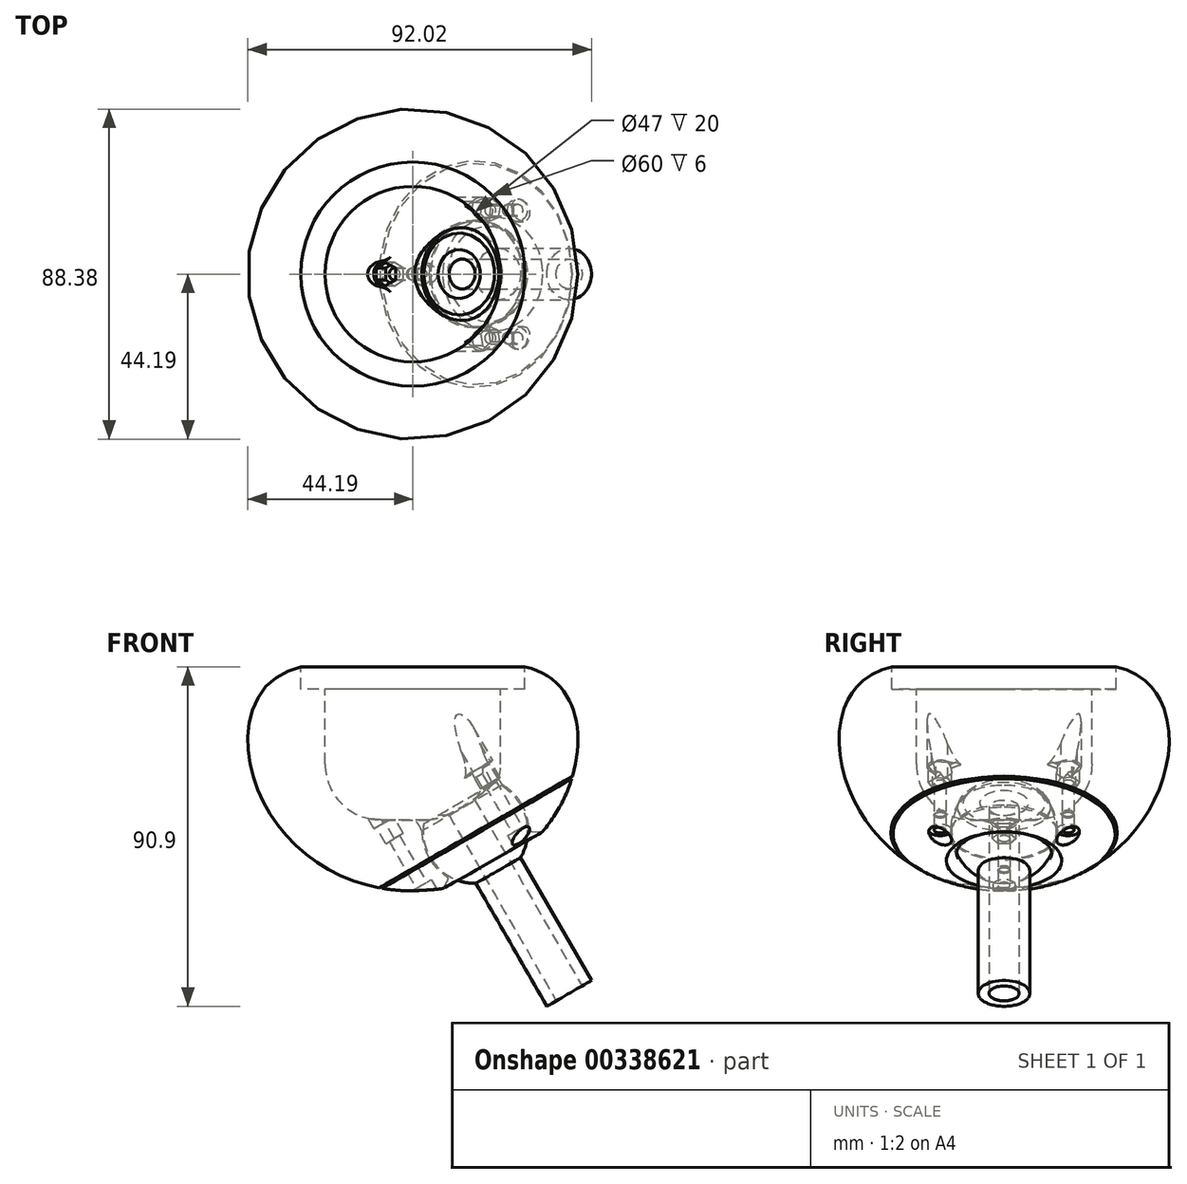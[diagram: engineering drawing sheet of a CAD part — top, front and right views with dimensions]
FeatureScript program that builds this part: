
annotation { "Feature Type Name" : "Feature", "Feature Type Description" : "" }
export const myFeature = defineFeature(function(context is Context, id is Id, definition is map)
    precondition{}
    {
        {
            var Q0;
            Q0=qCreatedBy(makeId("Front.planeOp"),FACE);
            var sketch = newSketch(context, id + "F0", { "sketchPlane" : qUnion([Q0])});
            skLineSegment(sketch, "E0", {"start": v(23.5, 32.37) * mm, "end": v(30, 32.37) * mm});
            skLineSegment(sketch, "E1", {"start": v(30, 32.37) * mm, "end": v(30, 38.37) * mm});
            skLineSegment(sketch, "E2", {"start": v(23.5, 32.37) * mm, "end": v(23.5, 12.37) * mm});
            skLineSegment(sketch, "E3", {"start": v(8.5, -2.63) * mm, "end": v(0, -2.63) * mm});
            skArc(sketch, "E4.filletArc", {"start": v(8.5, -2.63) * mm, "mid": v(19.1, 1.77) * mm, "end": v(23.5, 12.37) * mm});
            skLineSegment(sketch, "E5", {"start": v(43, 48.23) * mm, "end": v(43, -18) * mm, "construction": true});
            skLineSegment(sketch, "E6", {"start": v(0, 64.06) * mm, "end": v(0, 13.27) * mm, "construction": true});
            skPoint(sketch, "E7", {"position": v(43, 36.55) * mm});
            skPoint(sketch, "E8", {"position": v(43, 10.04) * mm});
            skFitSpline(sketch, "E9", {"points": [v(30, 38.37) * mm, v(43, 10.04) * mm, v(0, -21.63) * mm], "startDerivative": vector(90.04, -20.78) * mm, "endDerivative": vector(-121.99, 0) * mm});
            skPoint(sketch, "E10", {"position": v(30, 35.37) * mm});
            skLineSegment(sketch, "E11", {"start": v(0, -2.63) * mm, "end": v(0, -21.63) * mm});
            skSolve(sketch);
        }
        {
            var Q0;
            Q0=qCreatedBy(makeId("Front.planeOp"),FACE);
            var sketch = newSketch(context, id + "F1", { "sketchPlane" : qUnion([Q0])});
            skArc(sketch, "E12", {"start": v(31.35, -6.1) * mm, "mid": v(24.2, 6.35) * mm, "end": v(9.84, 6.36) * mm});
            skLineSegment(sketch, "E13", {"start": v(31.35, -6.1) * mm, "end": v(53.04, -7.04) * mm});
            skLineSegment(sketch, "E14", {"start": v(53.04, -7.04) * mm, "end": v(26.44, -22.4) * mm});
            skLineSegment(sketch, "E15", {"start": v(26.44, -22.4) * mm, "end": v(9.84, 6.36) * mm});
            skLineSegment(sketch, "E16", {"start": v(45.56, -47.51) * mm, "end": v(16.88, 2.16) * mm});
            skLineSegment(sketch, "E17", {"start": v(16.88, 2.16) * mm, "end": v(18.37, 4.75) * mm});
            skArc(sketch, "E18", {"start": v(29.08, -13.15) * mm, "mid": v(30.25, -1.52) * mm, "end": v(22.2, 6.95) * mm});
            skLineSegment(sketch, "E19", {"start": v(29.08, -13.15) * mm, "end": v(48.08, -46.06) * mm});
            skLineSegment(sketch, "E20", {"start": v(48.08, -46.06) * mm, "end": v(45.56, -47.51) * mm});
            skCircle(sketch, "E21", {"center": v(0, 23.4) * mm, "radius": 45.03 * mm, "construction": true});
            skLineSegment(sketch, "E22", {"start": v(18.37, 4.75) * mm, "end": v(22.2, 6.95) * mm});
            skArc(sketch, "E23", {"start": v(22.38, 13.92) * mm, "mid": v(22.45, 9.93) * mm, "end": v(24.2, 6.35) * mm});
            skLineSegment(sketch, "E24", {"start": v(22.38, 13.92) * mm, "end": v(9.84, 6.36) * mm});
            skLineSegment(sketch, "E25", {"start": v(-20.59, -27.76) * mm, "end": v(69.48, 24.24) * mm, "construction": true});
            skSolve(sketch);
        }
        {
            var Q0;
            Q0=qCreatedBy(makeId("Front.planeOp"),FACE);
            var sketch = newSketch(context, id + "F2", { "sketchPlane" : qUnion([Q0])});
            skLineSegment(sketch, "E26", {"start": v(-20.46, -27.98) * mm, "end": v(-20.71, -27.55) * mm});
            skLineSegment(sketch, "E27", {"start": v(-20.71, -27.55) * mm, "end": v(69.35, 24.45) * mm});
            skLineSegment(sketch, "E28", {"start": v(69.35, 24.45) * mm, "end": v(69.6, 24.02) * mm});
            skLineSegment(sketch, "E29", {"start": v(69.6, 24.02) * mm, "end": v(-20.46, -27.98) * mm});
            skSolve(sketch);
        }
        {
            var Q0;
            Q0=makeQuery(id+"F0.imprint","IMPRINT",FACE,{"disambiguationData":[TD([[makeQuery(id+"F0.imprint","IMPRINT",EDGE,{"derivedFrom":sQuery(id+"F0.wireOp",EDGE,"E0")}),-1.0]])]});
            var Q1;
            {var subQ6=sQuery(id+"F0.wireOp",EDGE,"E3");Q1=makeQuery(id+"F0.imprint","IMPRINT",FACE,{"disambiguationData":[TD([[makeQuery(id+"F0.imprint","IMPRINT",EDGE,{"derivedFrom":subQ6}),1.0]])]});}
            var Q2;
            {var subQ1=sQuery(id+"F0.wireOp",EDGE,"KXl2rAyY-RLrS-Eotx-2UTr-zvvv9nwZEpHV");var subQ3=sQuery(id+"F0.wireOp",EDGE,"E4.filletArc");var subQ4=makeQuery(id+"F0.imprint","INTERSECT",VERTEX,{"derivedFrom":[subQ3,subQ1]});Q2=makeQuery(id+"F0.imprint","IMPRINT",FACE,{"disambiguationData":[TD([[makeQuery(id+"F0.imprint","IMPRINT",EDGE,{"disambiguationData":[TD([[subQ4,1.0]])],"derivedFrom":subQ3}),-1.0]])]});}
            var Q3;
            {var subQ0=sQuery(id+"F0.wireOp",EDGE,"lHVRG2s5-drey-582v-L7Ij-X5NfUEFu1qqW");var subQ3=sQuery(id+"F0.wireOp",EDGE,"E4.filletArc");var subQ4=makeQuery(id+"F0.imprint","INTERSECT",VERTEX,{"derivedFrom":[subQ3,subQ0]});Q3=makeQuery(id+"F0.imprint","IMPRINT",FACE,{"disambiguationData":[TD([[makeQuery(id+"F0.imprint","IMPRINT",EDGE,{"disambiguationData":[TD([[subQ4,-1.0]])],"derivedFrom":subQ3}),-1.0]])]});}
            var Q4;
            {var subQ5=sQuery(id+"F0.wireOp",EDGE,"lHVRG2s5-drey-582v-L7Ij-X5NfUEFu1qqW");Q4=makeQuery(id+"F0.imprint","IMPRINT",FACE,{"disambiguationData":[TD([[makeQuery(id+"F0.imprint","IMPRINT",EDGE,{"derivedFrom":subQ5}),-1.0]])]});}
            var Q5;
            Q5=sQuery(id+"F0.wireOp",EDGE,"E6");
            revolve(context, id + "F3", {"entities" : qUnion([Q0, Q1, Q2, Q3, Q4]), "axis" : qUnion([Q5]), "revolveType" : RevolveType.FULL});
        }
        {
            var Q0;
            Q0=qSketchRegion(id+"F2",true);
            extrude(context, id + "F4", {"entities" : qUnion([Q0]), "operationType" : NewBodyOperationType.REMOVE, "endBound" : BoundingType.THROUGH_ALL, "oppositeDirection" : true, "depth" : 25 * mm, "hasSecondDirection" : true, "secondDirectionBound" : BoundingType.THROUGH_ALL, "secondDirectionOppositeDirection" : false, "secondDirectionDepth" : 25 * mm});
        }
        {
            var Q0;
            Q0=makeQuery(id+"F4.boolean.opBoolean","SPLIT",BODY,{"disambiguationData":[OD(1.0)],"derivedFrom":makeQuery(id+"F3.opRevolve","SWEPT_BODY",BODY,{"disambiguationData":[OSD([sQuery(id+"F0.wireOp",EDGE,"E0"),sQuery(id+"F0.wireOp",EDGE,"E1"),sQuery(id+"F0.wireOp",EDGE,"E2"),sQuery(id+"F0.wireOp",EDGE,"E3"),sQuery(id+"F0.wireOp",EDGE,"E4.filletArc"),sQuery(id+"F0.wireOp",EDGE,"E9"),sQuery(id+"F0.wireOp",EDGE,"E11")])]})});
            var Q1;
            Q1=sQuery(id+"F1.wireOp",EDGE,"E15");
            transform(context, id + "F5", {"entities" : qUnion([Q0]), "transformType" : TransformType.TRANSLATION_DISTANCE, "transformDirection" : qUnion([Q1]), "distance" : 0.5 * mm, "oppositeDirection" : true, "makeCopy" : false});
        }
        {
            var Q0;
            {var subQ0=sQuery(id+"F1.wireOp",EDGE,"E23");var subQ1=sQuery(id+"F1.wireOp",EDGE,"E12");var subQ2=makeQuery(id+"F1.imprint","INTERSECT",VERTEX,{"disambiguationData":[OD(1.0)],"derivedFrom":[subQ1,subQ0]});Q0=makeQuery(id+"F1.imprint","IMPRINT",FACE,{"disambiguationData":[TD([[makeQuery(id+"F1.imprint","IMPRINT",EDGE,{"disambiguationData":[TD([[subQ2,-1.0]])],"derivedFrom":subQ1}),-1.0]])]});}
            var Q1;
            {var subQ8=sQuery(id+"F1.wireOp",EDGE,"E13");Q1=makeQuery(id+"F1.imprint","IMPRINT",FACE,{"disambiguationData":[TD([[makeQuery(id+"F1.imprint","IMPRINT",EDGE,{"derivedFrom":subQ8}),-1.0]])]});}
            var Q2;
            {var subQ1=sQuery(id+"F1.wireOp",EDGE,"E17");Q2=makeQuery(id+"F1.imprint","IMPRINT",FACE,{"disambiguationData":[TD([[makeQuery(id+"F1.imprint","IMPRINT",EDGE,{"derivedFrom":subQ1}),-1.0]])]});}
            var Q3;
            Q3=sQuery(id+"F1.wireOp",EDGE,"E15");
            revolve(context, id + "F6", {"operationType" : NewBodyOperationType.REMOVE, "entities" : qUnion([Q0, Q1, Q2]), "axis" : qUnion([Q3]), "revolveType" : RevolveType.FULL, "oppositeDirection" : true});
        }
        {
            var Q0;
            {var subQ1=sQuery(id+"F1.wireOp",EDGE,"E17");Q0=makeQuery(id+"F1.imprint","IMPRINT",FACE,{"disambiguationData":[TD([[makeQuery(id+"F1.imprint","IMPRINT",EDGE,{"derivedFrom":subQ1}),-1.0]])]});}
            var Q1;
            {var subQ5=sQuery(id+"F1.wireOp",EDGE,"E20");Q1=makeQuery(id+"F1.imprint","IMPRINT",FACE,{"disambiguationData":[TD([[makeQuery(id+"F1.imprint","IMPRINT",EDGE,{"derivedFrom":subQ5}),-1.0]])]});}
            var Q2;
            Q2=sQuery(id+"F1.wireOp",EDGE,"E15");
            revolve(context, id + "F7", {"entities" : qUnion([Q0, Q1]), "axis" : qUnion([Q2]), "revolveType" : RevolveType.FULL});
        }
        {
            var Q0;
            Q0=makeQuery(id+"F6.boolean.opBoolean","COPY",EDGE,{"derivedFrom":makeQuery(id+"F6.opRevolve","SWEPT_EDGE",EDGE,{"disambiguationData":[OSD([sQuery(id+"F1.wireOp",EDGE,"E12"),sQuery(id+"F1.wireOp",EDGE,"E13")])]})});
            var Q1;
            Q1=makeQuery(id+"F6.boolean.opBoolean","INTERSECT",EDGE,{"derivedFrom":[makeQuery(id+"F3.opRevolve","SWEPT_FACE",FACE,{"disambiguationData":[OSD([sQuery(id+"F0.wireOp",EDGE,"E4.filletArc")])]}),makeQuery(id+"F6.opRevolve","SWEPT_FACE",FACE,{"disambiguationData":[OSD([sQuery(id+"F1.wireOp",EDGE,"E12")])]})]});
            fillet(context, id + "F8", {"entities" : qUnion([Q0, Q1]), "radius" : 1 * mm, "tangentPropagation" : true, "allowEdgeOverflow" : false});
        }
        {
            var Q0;
            Q0=makeQuery(id+"F4.boolean.opBoolean","COPY",FACE,{"derivedFrom":makeQuery(id+"F4.opExtrude","SWEPT_FACE",FACE,{"disambiguationData":[OSD([sQuery(id+"F2.wireOp",EDGE,"E27")])]})});
            cPlane(context, id + "F9", {"entities" : qUnion([Q0]), "cplaneType" : CPlaneType.OFFSET, "offset" : 16.6 * mm, "width" : 150 * mm, "height" : 150 * mm});
        }
        {
            var Q0;
            Q0=qCreatedBy(id+"F9.planeOp",FACE);
            var sketch = newSketch(context, id + "F10", { "sketchPlane" : qUnion([Q0])});
            skLineSegment(sketch, "E30", {"start": v(-2.62, 0) * mm, "end": v(-18.22, 0) * mm, "construction": true});
            skCircle(sketch, "E31", {"center": v(-8.07, 0) * mm, "radius": 1.6 * mm});
            skCircle(sketch, "E32", {"center": v(-8.07, 0) * mm, "radius": 3.05 * mm});
            skPoint(sketch, "E33", {"position": v(11.7, 0) * mm});
            skCircle(sketch, "E34.1.0", {"center": v(21.6, -17.13) * mm, "radius": 3.05 * mm});
            skCircle(sketch, "E34.1.1", {"center": v(21.6, -17.13) * mm, "radius": 1.6 * mm});
            skCircle(sketch, "E34.2.0", {"center": v(21.6, 17.13) * mm, "radius": 3.05 * mm});
            skCircle(sketch, "E34.2.1", {"center": v(21.6, 17.13) * mm, "radius": 1.6 * mm});
            skSolve(sketch);
        }
        {
            var Q0;
            Q0=makeQuery(id+"F10.imprint","IMPRINT",FACE,{"disambiguationData":[TD([[makeQuery(id+"F10.imprint","IMPRINT",EDGE,{"derivedFrom":sQuery(id+"F10.wireOp",EDGE,"E34.2.1")}),1.0]])]});
            var Q1;
            Q1=makeQuery(id+"F10.imprint","IMPRINT",FACE,{"disambiguationData":[TD([[makeQuery(id+"F10.imprint","IMPRINT",EDGE,{"derivedFrom":sQuery(id+"F10.wireOp",EDGE,"E34.1.1")}),1.0]])]});
            var Q2;
            Q2=makeQuery(id+"F10.imprint","IMPRINT",FACE,{"disambiguationData":[TD([[makeQuery(id+"F10.imprint","IMPRINT",EDGE,{"derivedFrom":sQuery(id+"F10.wireOp",EDGE,"E31")}),1.0]])]});
            extrude(context, id + "F11", {"entities" : qUnion([Q0, Q1, Q2]), "operationType" : NewBodyOperationType.REMOVE, "oppositeDirection" : true, "depth" : 31 * mm});
        }
        {
            var Q0;
            Q0=makeQuery(id+"F10.imprint","IMPRINT",FACE,{"disambiguationData":[TD([[makeQuery(id+"F10.imprint","IMPRINT",EDGE,{"derivedFrom":sQuery(id+"F10.wireOp",EDGE,"E34.1.0")}),1.0]])]});
            var Q1;
            Q1=makeQuery(id+"F10.imprint","IMPRINT",FACE,{"disambiguationData":[TD([[makeQuery(id+"F10.imprint","IMPRINT",EDGE,{"derivedFrom":sQuery(id+"F10.wireOp",EDGE,"E31")}),-1.0]])]});
            var Q2;
            Q2=makeQuery(id+"F10.imprint","IMPRINT",FACE,{"disambiguationData":[TD([[makeQuery(id+"F10.imprint","IMPRINT",EDGE,{"derivedFrom":sQuery(id+"F10.wireOp",EDGE,"E34.2.0")}),1.0]])]});
            extrude(context, id + "F12", {"entities" : qUnion([Q0, Q1, Q2]), "operationType" : NewBodyOperationType.REMOVE, "oppositeDirection" : true, "depth" : 11.5 * mm});
        }
        {
            var Q0;
            Q0=makeQuery(id+"F11.boolean.opBoolean","COPY",FACE,{"derivedFrom":makeQuery(id+"F11.opExtrude","CAP_FACE",FACE,{"disambiguationData":[OSD([sQuery(id+"F10.wireOp",EDGE,"E31")])],"isStart":false})});
            cPlane(context, id + "F13", {"entities" : qUnion([Q0]), "cplaneType" : CPlaneType.OFFSET, "offset" : 0 * mm, "oppositeDirection" : true, "width" : 150 * mm, "height" : 150 * mm});
        }
        {
            var Q0;
            Q0=qCreatedBy(id+"F13.planeOp",FACE);
            var sketch = newSketch(context, id + "F14", { "sketchPlane" : qUnion([Q0])});
            skCircle(sketch, "E35.cCircle", {"center": v(21.6, 17.13) * mm, "radius": 2.75 * mm, "construction": true});
            skLineSegment(sketch, "E35.0", {"start": v(22.16, 20.25) * mm, "end": v(24.58, 18.2) * mm});
            skLineSegment(sketch, "E35.1", {"start": v(24.58, 18.2) * mm, "end": v(24.01, 15.07) * mm});
            skLineSegment(sketch, "E35.2", {"start": v(24.01, 15.07) * mm, "end": v(21.03, 14) * mm});
            skLineSegment(sketch, "E35.3", {"start": v(21.03, 14) * mm, "end": v(18.6, 16.05) * mm});
            skLineSegment(sketch, "E35.4", {"start": v(18.6, 16.05) * mm, "end": v(19.17, 19.18) * mm});
            skLineSegment(sketch, "E35.5", {"start": v(19.17, 19.18) * mm, "end": v(22.16, 20.25) * mm});
            skPoint(sketch, "E35.0.midPoint", {"position": v(23.37, 19.22) * mm});
            skCircle(sketch, "E36.cCircle", {"center": v(-8.07, 0) * mm, "radius": 2.75 * mm, "construction": true});
            skLineSegment(sketch, "E36.0", {"start": v(-10.82, -1.59) * mm, "end": v(-10.82, 1.59) * mm});
            skLineSegment(sketch, "E36.1", {"start": v(-10.82, 1.59) * mm, "end": v(-8.07, 3.18) * mm});
            skLineSegment(sketch, "E36.2", {"start": v(-8.07, 3.18) * mm, "end": v(-5.32, 1.59) * mm});
            skLineSegment(sketch, "E36.3", {"start": v(-5.32, 1.59) * mm, "end": v(-5.32, -1.59) * mm});
            skLineSegment(sketch, "E36.4", {"start": v(-5.32, -1.59) * mm, "end": v(-8.07, -3.18) * mm});
            skLineSegment(sketch, "E36.5", {"start": v(-8.07, -3.18) * mm, "end": v(-10.82, -1.59) * mm});
            skPoint(sketch, "E36.0.midPoint", {"position": v(-10.82, 0) * mm});
            skLineSegment(sketch, "E37", {"start": v(11.7, 0) * mm, "end": v(42.27, 0) * mm, "construction": true});
            skLineSegment(sketch, "E38.MirrorCS", {"start": v(22.16, -20.25) * mm, "end": v(24.58, -18.2) * mm});
            skLineSegment(sketch, "E39.MirrorCS", {"start": v(21.03, -14) * mm, "end": v(18.6, -16.05) * mm});
            skPoint(sketch, "E40.MirrorP", {"position": v(23.37, -19.22) * mm});
            skLineSegment(sketch, "E41.MirrorCS", {"start": v(24.01, -15.07) * mm, "end": v(21.03, -14) * mm});
            skLineSegment(sketch, "E42.MirrorCS", {"start": v(24.58, -18.2) * mm, "end": v(24.01, -15.07) * mm});
            skLineSegment(sketch, "E43.MirrorCS", {"start": v(18.6, -16.05) * mm, "end": v(19.17, -19.18) * mm});
            skLineSegment(sketch, "E44.MirrorCS", {"start": v(19.17, -19.18) * mm, "end": v(22.16, -20.25) * mm});
            skCircle(sketch, "E45.MirrorC", {"center": v(21.6, -17.13) * mm, "radius": 2.75 * mm, "construction": true});
            skSolve(sketch);
        }
        {
            var Q0;
            Q0=qSketchRegion(id+"F14",true);
            extrude(context, id + "F15", {"entities" : qUnion([Q0]), "operationType" : NewBodyOperationType.REMOVE, "depth" : 5 * mm});
        }
        {
            var Q0;
            Q0=qCreatedBy(id+"F13.planeOp",FACE);
            var sketch = newSketch(context, id + "F16", { "sketchPlane" : qUnion([Q0])});
            skCircle(sketch, "E46.2.0", {"center": v(21.6, -17.13) * mm, "radius": 3.5 * mm});
            skArc(sketch, "E47", {"start": v(19.04, -19.52) * mm, "mid": v(15.95, -18.24) * mm, "end": v(12.76, -19.26) * mm});
            skArc(sketch, "E48", {"start": v(25.13, -8.5) * mm, "mid": v(23.8, -11.72) * mm, "end": v(24.47, -15.14) * mm});
            skLineSegment(sketch, "E49", {"start": v(25.13, -8.5) * mm, "end": v(12.76, -19.26) * mm});
            skPoint(sketch, "E50", {"position": v(11.7, 0) * mm});
            skArc(sketch, "E51.MirrorCS", {"start": v(19.04, 19.52) * mm, "mid": v(15.95, 18.24) * mm, "end": v(12.76, 19.26) * mm});
            skArc(sketch, "E52.MirrorCS", {"start": v(25.13, 8.5) * mm, "mid": v(23.8, 11.72) * mm, "end": v(24.47, 15.14) * mm});
            skLineSegment(sketch, "E53.MirrorCS", {"start": v(25.13, 8.5) * mm, "end": v(12.76, 19.26) * mm});
            skCircle(sketch, "E54.MirrorC", {"center": v(21.6, 17.13) * mm, "radius": 3.5 * mm});
            skCircle(sketch, "E55", {"center": v(-8.07, 0) * mm, "radius": 3.5 * mm});
            skArc(sketch, "E56", {"start": v(-5.4, -6.7) * mm, "mid": v(-6.42, -4.63) * mm, "end": v(-8.43, -3.48) * mm});
            skArc(sketch, "E57", {"start": v(-8.58, 3.46) * mm, "mid": v(-6.35, 4.99) * mm, "end": v(-5.63, 7.6) * mm});
            skLineSegment(sketch, "E58", {"start": v(-5.4, -6.7) * mm, "end": v(-5.63, 7.6) * mm});
            skSolve(sketch);
        }
        {
            var Q0;
            Q0=qSketchRegion(id+"F16",true);
            extrude(context, id + "F17", {"entities" : qUnion([Q0]), "operationType" : NewBodyOperationType.REMOVE, "oppositeDirection" : true, "depth" : 17.6 * mm});
        }
        {
            var Q0;
            Q0=makeQuery(id+"F17.boolean.opBoolean","INTERSECT",EDGE,{"disambiguationData":[OD(1.0)],"derivedFrom":[makeQuery(id+"F3.opRevolve","SWEPT_FACE",FACE,{"disambiguationData":[OSD([sQuery(id+"F0.wireOp",EDGE,"E4.filletArc")])]}),makeQuery(id+"F17.opExtrude","CAP_FACE",FACE,{"disambiguationData":[OSD([sQuery(id+"F16.wireOp",EDGE,"E46.2.0"),sQuery(id+"F16.wireOp",EDGE,"E47"),sQuery(id+"F16.wireOp",EDGE,"E48"),sQuery(id+"F16.wireOp",EDGE,"E49")])],"isStart":true})]});
            var Q1;
            Q1=makeQuery(id+"F17.boolean.opBoolean","INTERSECT",EDGE,{"disambiguationData":[OD(0.0)],"derivedFrom":[makeQuery(id+"F3.opRevolve","SWEPT_FACE",FACE,{"disambiguationData":[OSD([sQuery(id+"F0.wireOp",EDGE,"E4.filletArc")])]}),makeQuery(id+"F17.opExtrude","CAP_FACE",FACE,{"disambiguationData":[OSD([sQuery(id+"F16.wireOp",EDGE,"E46.2.0"),sQuery(id+"F16.wireOp",EDGE,"E47"),sQuery(id+"F16.wireOp",EDGE,"E48"),sQuery(id+"F16.wireOp",EDGE,"E49")])],"isStart":true})]});
            var Q2;
            Q2=makeQuery(id+"F17.boolean.opBoolean","INTERSECT",EDGE,{"disambiguationData":[OD(1.0)],"derivedFrom":[makeQuery(id+"F3.opRevolve","SWEPT_FACE",FACE,{"disambiguationData":[OSD([sQuery(id+"F0.wireOp",EDGE,"E3")])]}),makeQuery(id+"F17.opExtrude","CAP_FACE",FACE,{"disambiguationData":[OSD([sQuery(id+"F16.wireOp",EDGE,"E55"),sQuery(id+"F16.wireOp",EDGE,"E56"),sQuery(id+"F16.wireOp",EDGE,"E57"),sQuery(id+"F16.wireOp",EDGE,"E58")])],"isStart":true})]});
            var Q3;
            Q3=makeQuery(id+"F17.boolean.opBoolean","INTERSECT",EDGE,{"disambiguationData":[OD(0.0)],"derivedFrom":[makeQuery(id+"F3.opRevolve","SWEPT_FACE",FACE,{"disambiguationData":[OSD([sQuery(id+"F0.wireOp",EDGE,"E3")])]}),makeQuery(id+"F17.opExtrude","CAP_FACE",FACE,{"disambiguationData":[OSD([sQuery(id+"F16.wireOp",EDGE,"E55"),sQuery(id+"F16.wireOp",EDGE,"E56"),sQuery(id+"F16.wireOp",EDGE,"E57"),sQuery(id+"F16.wireOp",EDGE,"E58")])],"isStart":true})]});
            var Q4;
            Q4=makeQuery(id+"F17.boolean.opBoolean","INTERSECT",EDGE,{"disambiguationData":[OD(0.0)],"derivedFrom":[makeQuery(id+"F3.opRevolve","SWEPT_FACE",FACE,{"disambiguationData":[OSD([sQuery(id+"F0.wireOp",EDGE,"E4.filletArc")])]}),makeQuery(id+"F17.opExtrude","CAP_FACE",FACE,{"disambiguationData":[OSD([sQuery(id+"F16.wireOp",EDGE,"E51.MirrorCS"),sQuery(id+"F16.wireOp",EDGE,"E52.MirrorCS"),sQuery(id+"F16.wireOp",EDGE,"E53.MirrorCS"),sQuery(id+"F16.wireOp",EDGE,"E54.MirrorC")])],"isStart":true})]});
            var Q5;
            Q5=makeQuery(id+"F17.boolean.opBoolean","INTERSECT",EDGE,{"disambiguationData":[OD(1.0)],"derivedFrom":[makeQuery(id+"F3.opRevolve","SWEPT_FACE",FACE,{"disambiguationData":[OSD([sQuery(id+"F0.wireOp",EDGE,"E4.filletArc")])]}),makeQuery(id+"F17.opExtrude","CAP_FACE",FACE,{"disambiguationData":[OSD([sQuery(id+"F16.wireOp",EDGE,"E51.MirrorCS"),sQuery(id+"F16.wireOp",EDGE,"E52.MirrorCS"),sQuery(id+"F16.wireOp",EDGE,"E53.MirrorCS"),sQuery(id+"F16.wireOp",EDGE,"E54.MirrorC")])],"isStart":true})]});
            fillet(context, id + "F18", {"entities" : qUnion([Q0, Q1, Q2, Q3, Q4, Q5]), "radius" : 1 * mm, "tangentPropagation" : true, "allowEdgeOverflow" : false});
        }
    });
